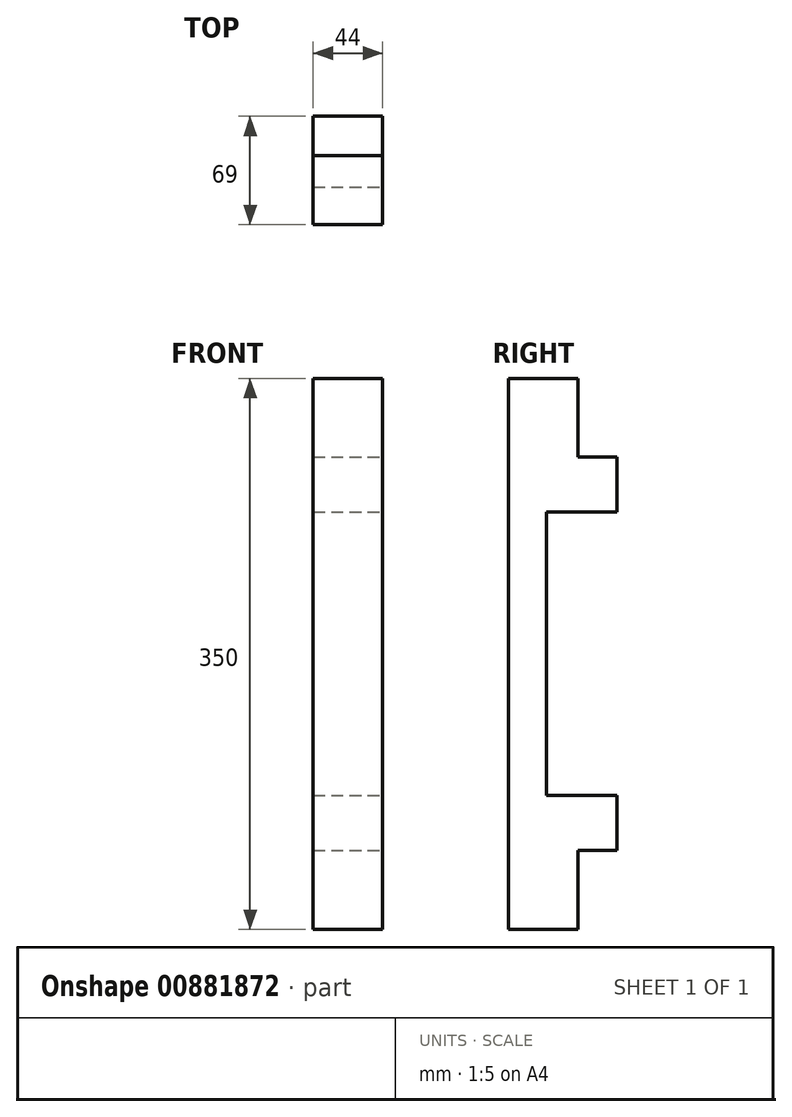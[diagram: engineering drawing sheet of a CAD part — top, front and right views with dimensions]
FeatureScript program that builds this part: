
annotation { "Feature Type Name" : "Feature", "Feature Type Description" : "" }
export const myFeature = defineFeature(function(context is Context, id is Id, definition is map)
    precondition{}
    {
        {
            var Q0;
            Q0=qCreatedBy(makeId("Top.planeOp"),FACE);
            var sketch = newSketch(context, id + "F0", { "sketchPlane" : qUnion([Q0])});
            skLineSegment(sketch, "E0.bottom", {"start": v(22, -34.5) * mm, "end": v(-22, -34.5) * mm});
            skLineSegment(sketch, "E0.top", {"start": v(22, 34.5) * mm, "end": v(-22, 34.5) * mm});
            skLineSegment(sketch, "E0.left", {"start": v(22, -34.5) * mm, "end": v(22, 34.5) * mm});
            skLineSegment(sketch, "E0.right", {"start": v(-22, -34.5) * mm, "end": v(-22, 34.5) * mm});
            skPoint(sketch, "E0.middle", {"position": v(0, 0) * mm});
            skSolve(sketch);
        }
        {
            var Q0;
            Q0=qSketchRegion(id+"F0",true);
            extrude(context, id + "F1", {"entities" : qUnion([Q0]), "depth" : 350 * mm, "offsetDistance" : 25 * mm});
        }
        {
            var Q0;
            Q0=makeQuery(id+"F1.opExtrude","SWEPT_FACE",FACE,{"disambiguationData":[OSD([sQuery(id+"F0.wireOp",EDGE,"E0.left")])]});
            var sketch = newSketch(context, id + "F2", { "sketchPlane" : qUnion([Q0])});
            skLineSegment(sketch, "E1", {"start": v(34.5, 175) * mm, "end": v(-34.5, 175) * mm, "construction": true});
            skLineSegment(sketch, "E2", {"start": v(34.5, 85) * mm, "end": v(-10.5, 85) * mm});
            skLineSegment(sketch, "E3", {"start": v(-10.5, 85) * mm, "end": v(-10.5, 175) * mm});
            skLineSegment(sketch, "E4", {"start": v(34.5, 85) * mm, "end": v(34.5, 175) * mm});
            skLineSegment(sketch, "E5.MirrorCS", {"start": v(34.5, 265) * mm, "end": v(34.5, 175) * mm});
            skLineSegment(sketch, "E6.MirrorCS", {"start": v(34.5, 265) * mm, "end": v(-10.5, 265) * mm});
            skLineSegment(sketch, "E7.MirrorCS", {"start": v(-10.5, 265) * mm, "end": v(-10.5, 175) * mm});
            skLineSegment(sketch, "E8", {"start": v(9.5, 0) * mm, "end": v(9.5, 50) * mm});
            skLineSegment(sketch, "E9", {"start": v(9.5, 50) * mm, "end": v(34.5, 50) * mm});
            skLineSegment(sketch, "E10", {"start": v(9.5, 0) * mm, "end": v(34.5, 0) * mm});
            skLineSegment(sketch, "E11", {"start": v(34.5, 0) * mm, "end": v(34.5, 50) * mm});
            skLineSegment(sketch, "E12.MirrorCS", {"start": v(34.5, 350) * mm, "end": v(34.5, 300) * mm});
            skLineSegment(sketch, "E13.MirrorCS", {"start": v(9.5, 350) * mm, "end": v(34.5, 350) * mm});
            skLineSegment(sketch, "E14.MirrorCS", {"start": v(9.5, 350) * mm, "end": v(9.5, 300) * mm});
            skLineSegment(sketch, "E15.MirrorCS", {"start": v(9.5, 300) * mm, "end": v(34.5, 300) * mm});
            skSolve(sketch);
        }
        {
            var Q0;
            Q0=qSketchRegion(id+"F2",true);
            extrude(context, id + "F3", {"entities" : qUnion([Q0]), "operationType" : NewBodyOperationType.REMOVE, "endBound" : BoundingType.THROUGH_ALL, "oppositeDirection" : true, "depth" : 25 * mm, "offsetDistance" : 25 * mm});
        }
    });
